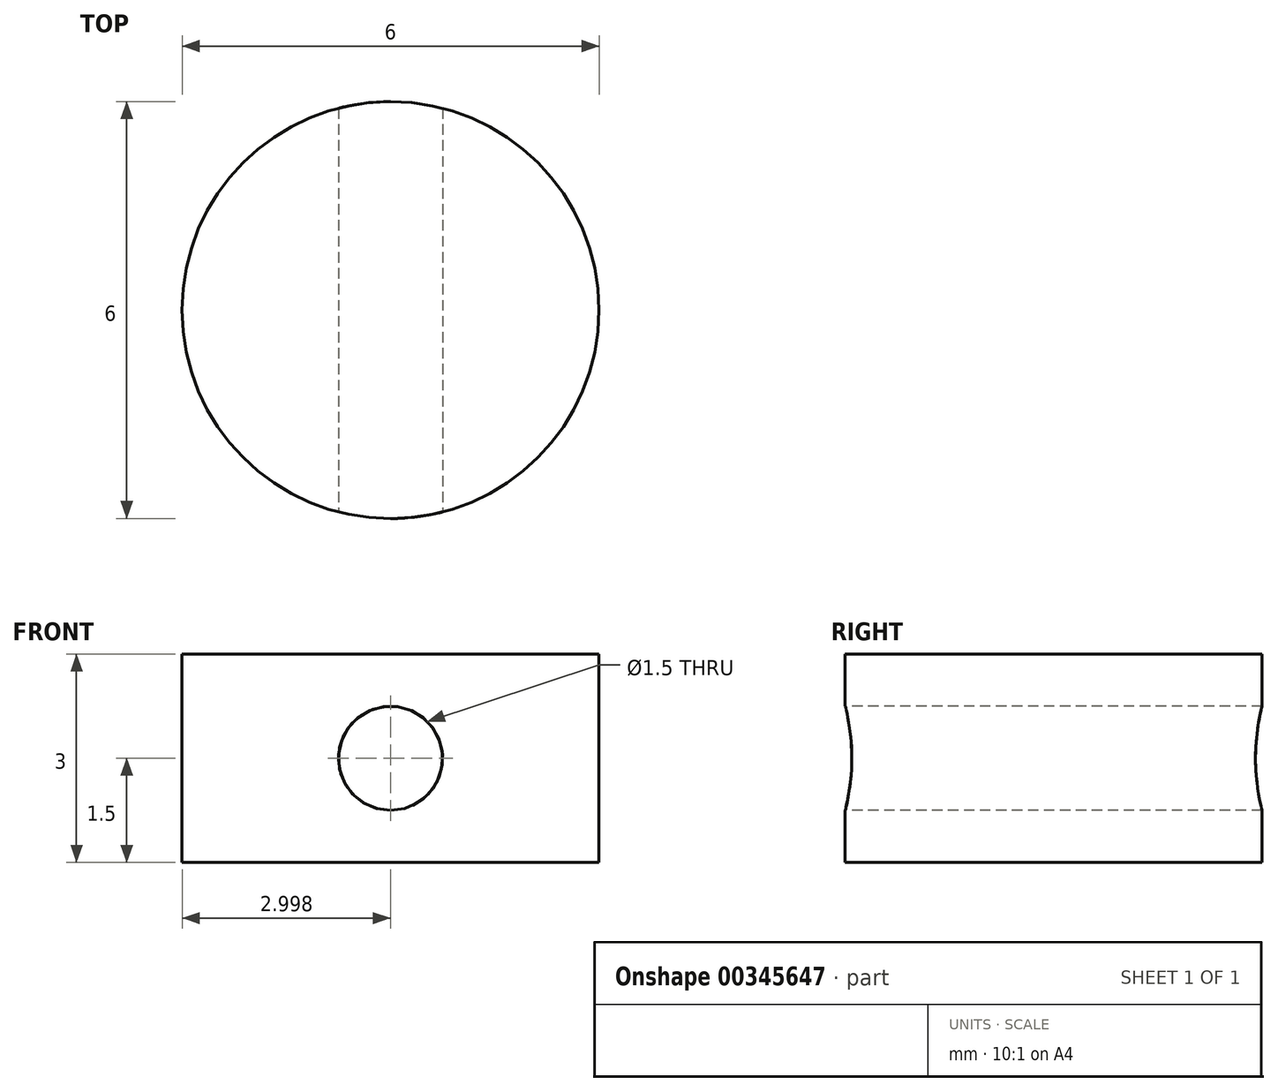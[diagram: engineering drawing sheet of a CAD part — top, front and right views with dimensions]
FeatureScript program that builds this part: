
annotation { "Feature Type Name" : "Feature", "Feature Type Description" : "" }
export const myFeature = defineFeature(function(context is Context, id is Id, definition is map)
    precondition{}
    {
        {
            var Q0;
            Q0=qCreatedBy(makeId("Front.planeOp"),FACE);
            var sketch = newSketch(context, id + "F0", { "sketchPlane" : qUnion([Q0])});
            skArc(sketch, "E0", {"start": v(-45.46, 6.4) * mm, "mid": v(-44.48, 4.44) * mm, "end": v(-42.46, 3.59) * mm});
            skLineSegment(sketch, "E1", {"start": v(-39.46, 0.59) * mm, "end": v(-39.46, 39.52) * mm, "construction": true});
            skLineSegment(sketch, "E2", {"start": v(-42.46, 3.59) * mm, "end": v(-39.46, 3.59) * mm});
            skSolve(sketch);
        }
        {
            var Q0;
            Q0=sQuery(id+"F0.wireOp",EDGE,"E0");
            var Q1;
            Q1=sQuery(id+"F0.wireOp",EDGE,"E2");
            var Q2;
            Q2=sQuery(id+"F0.wireOp",EDGE,"E1");
            revolve(context, id + "F1", {"bodyType" : ToolBodyType.SURFACE, "surfaceEntities" : qUnion([Q0, Q1]), "axis" : qUnion([Q2]), "revolveType" : RevolveType.FULL});
        }
        {
            var Q0;
            Q0=qCreatedBy(makeId("Top.planeOp"),FACE);
            var sketch = newSketch(context, id + "F2", { "sketchPlane" : qUnion([Q0])});
            skCircle(sketch, "E3", {"center": v(-39.46, 0) * mm, "radius": 3 * mm});
            skSolve(sketch);
        }
        {
            var Q0;
            Q0=qSketchRegion(id+"F2",true);
            extrude(context, id + "F3", {"entities" : qUnion([Q0]), "depth" : 3 * mm});
        }
        {
            var Q0;
            Q0=qCreatedBy(makeId("Front.planeOp"),FACE);
            var sketch = newSketch(context, id + "F4", { "sketchPlane" : qUnion([Q0])});
            skLineSegment(sketch, "E4", {"start": v(-39.46, 0) * mm, "end": v(-39.46, 3) * mm, "construction": true});
            skCircle(sketch, "E5", {"center": v(-39.46, 1.5) * mm, "radius": 0.75 * mm});
            skSolve(sketch);
        }
        {
            var Q0;
            Q0=makeQuery(id+"F4.imprint","IMPRINT",FACE,{"disambiguationData":[TD([[makeQuery(id+"F4.imprint","IMPRINT",EDGE,{"derivedFrom":sQuery(id+"F4.wireOp",EDGE,"E5")}),1.0]])]});
            var Q1;
            Q1=sQuery(id+"F4.wireOp",EDGE,"E5");
            extrude(context, id + "F5", {"entities" : qUnion([Q0]), "operationType" : NewBodyOperationType.REMOVE, "surfaceEntities" : qUnion([Q1]), "oppositeDirection" : true, "depth" : 6.62 * mm, "symmetric" : true});
        }
        {
            var Q0;
            Q0=makeQuery(id+"F3.opExtrude","CAP_FACE",FACE,{"disambiguationData":[OSD([sQuery(id+"F2.wireOp",EDGE,"E3")])],"isStart":false});
            var sketch = newSketch(context, id + "F6", { "sketchPlane" : qUnion([Q0])});
            skLineSegment(sketch, "E6", {"start": v(-39.42, -3) * mm, "end": v(-39.42, 3) * mm, "construction": true});
            skSolve(sketch);
        }
        {
            var Q0;
            Q0=sQuery(id+"F6.wireOp",EDGE,"E6");
            cPoint(context, id + "F7", {"entities" : qUnion([Q0]), "parameter" : 0.5});
        }
        {
            var Q0;
            Q0=makeQuery(id+"F3.opExtrude","SWEPT_BODY",BODY,{"disambiguationData":[OSD([sQuery(id+"F2.wireOp",EDGE,"E3")])]});
            var Q1;
            Q1=makeQuery(id+"F1.opRevolve","SWEPT_BODY",BODY,{"disambiguationData":[OSD([sQuery(id+"F0.wireOp",EDGE,"E2")])]});
            var Q2;
            Q2=sQuery(id+"F0.wireOp",VERTEX,"E2.end");
            var Q3;
            Q3=qCreatedBy(id+"F7",VERTEX);
            transform(context, id + "F8", {"entities" : qUnion([Q0, Q1]), "transformType" : TransformType.TRANSLATION_ENTITY, "oppositeDirectionEntity" : false, "transformLine" : qUnion([Q2, Q3]), "makeCopy" : false});
        }
    });
